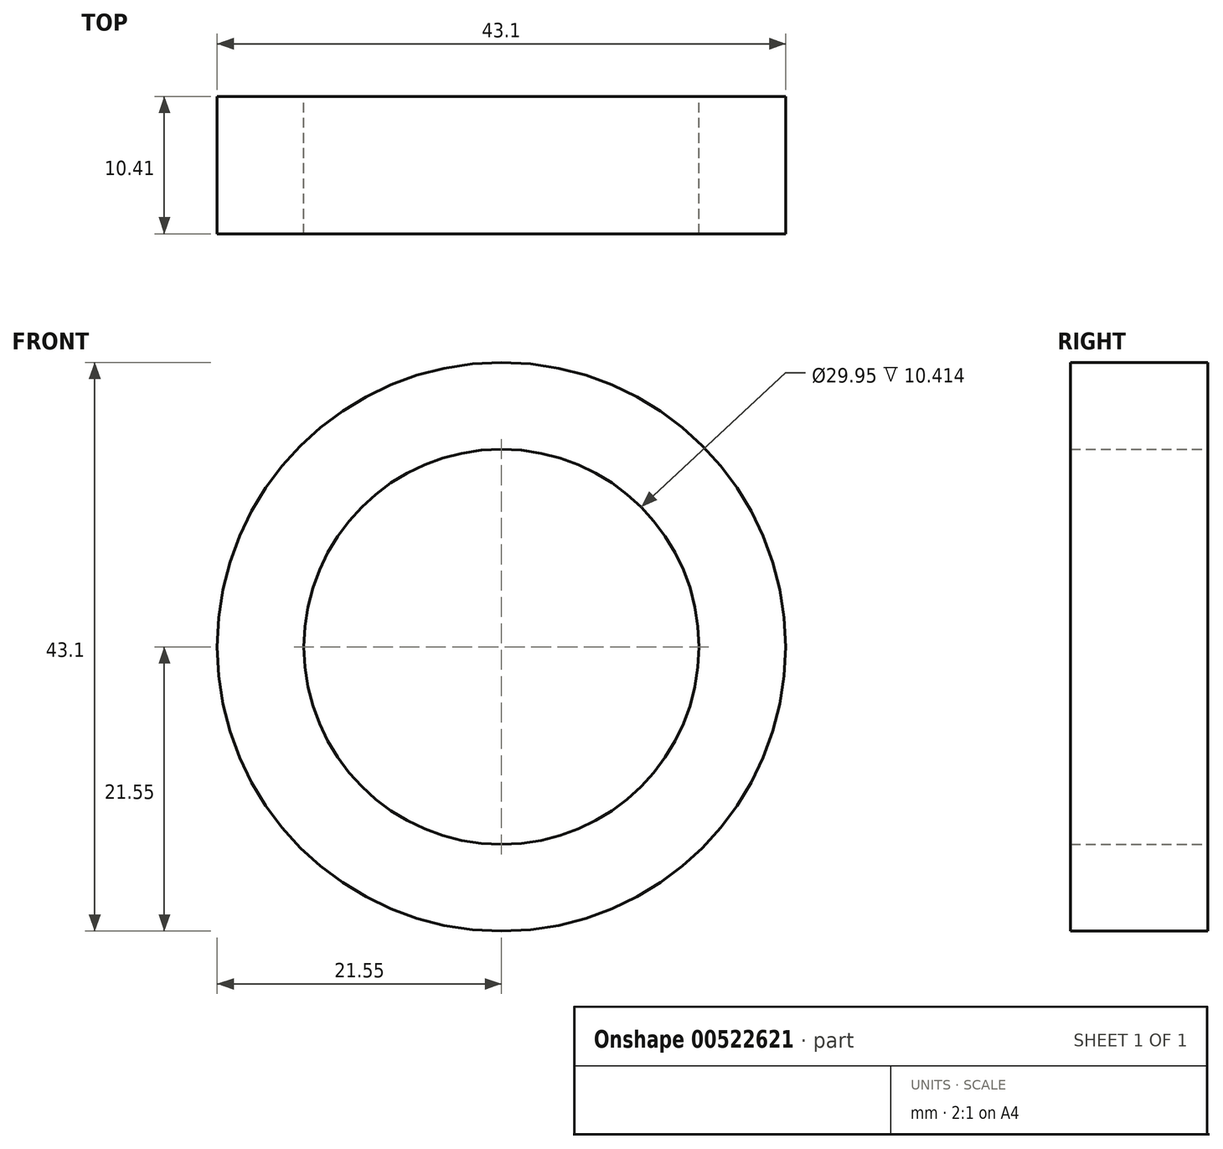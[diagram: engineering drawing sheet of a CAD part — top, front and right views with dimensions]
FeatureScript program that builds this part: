
annotation { "Feature Type Name" : "Feature", "Feature Type Description" : "" }
export const myFeature = defineFeature(function(context is Context, id is Id, definition is map)
    precondition{}
    {
        {
            var Q0;
            Q0=qCreatedBy(makeId("Front.planeOp"),FACE);
            var sketch = newSketch(context, id + "F0", { "sketchPlane" : qUnion([Q0])});
            skCircle(sketch, "E0", {"center": v(0, 0) * mm, "radius": 14.97 * mm});
            skCircle(sketch, "E1", {"center": v(0, 0) * mm, "radius": 21.55 * mm});
            skSolve(sketch);
        }
        {
            var Q0;
            Q0 = qSketchRegion(id + "F0", true);
            extrude(context, id + "F1", {"entities" : qUnion([Q0]), "depth" : 10.4 * mm, "offsetDistance" : 25.4 * mm});
        }
    });
